# Revit family: EDFPBV114C
name_source: partatom
category: Plumbing Fixtures
units: mm (PartAtom-declared; Revit-internal decimal feet)

## family parameters
Always vertical = Yes
Cut with Voids When Loaded = No
OmniClass Number = 23.45.00.00
OmniClass Title = Sanitary, Laundry, and Cleaning Equipment
Part Type = Normal
Room Calculation Point = No
Round Connector Dimension = Use Radius
Shared = No
Work Plane-Based = No

## types (1)
- EDFPBV114C
    Activation by = Mechanical Front Bubbler Button
    Approx. Shipping Weight = 18 lbs
    Body Material = Metal - Steel - Stainless - Chrome
    Bubbler Style = Vandal Resistant
    CW Connection = Yes
    Chilling Option = Non-refrigerated
    Date = 09-10-2020
    Description = SWIRLFLO VR FTN
    Dimensions (L x W x H) = 14 inch x 18 3/8 inch x 11 5/16 inch
    Finish = Stainless Steel
    HW Connection = No
    Installation Location = Indoor
    Manufacturer = Elkay
    Model = EDFPBV114C
    Mounting Type = Wall Mount (On Wall)
    N of Stations Served = 1
    Power = No Electrical Required
    Sanitary Connector Description = Sanitary Connection
    Sanitary Service Size Radius = 22 mm  [stored 0.0721785 ft]
    URL = https://www.elkay.com
    Vent Connection = No
    Version = 1.0.0.0
    Wall Plate Material = Metal - Steel - Stainless - Chrome
    Waste Connection = Yes
    Water Connector Description = Water Supply
    Water Out Connection Description = Water Return
    Water Service Flow = 0 GPM
    Water Service Flow Out = 0 GPM
    Water Service Size Radius = 11 mm  [stored 0.0360892 ft]

note: [stored X ft] marks values corroborated as IEEE doubles in the binary element streams (Revit-internal decimal feet)

## geometry (parser evidence)
native form markers: Sweep x27
no freeform markers — native parametric forms only
